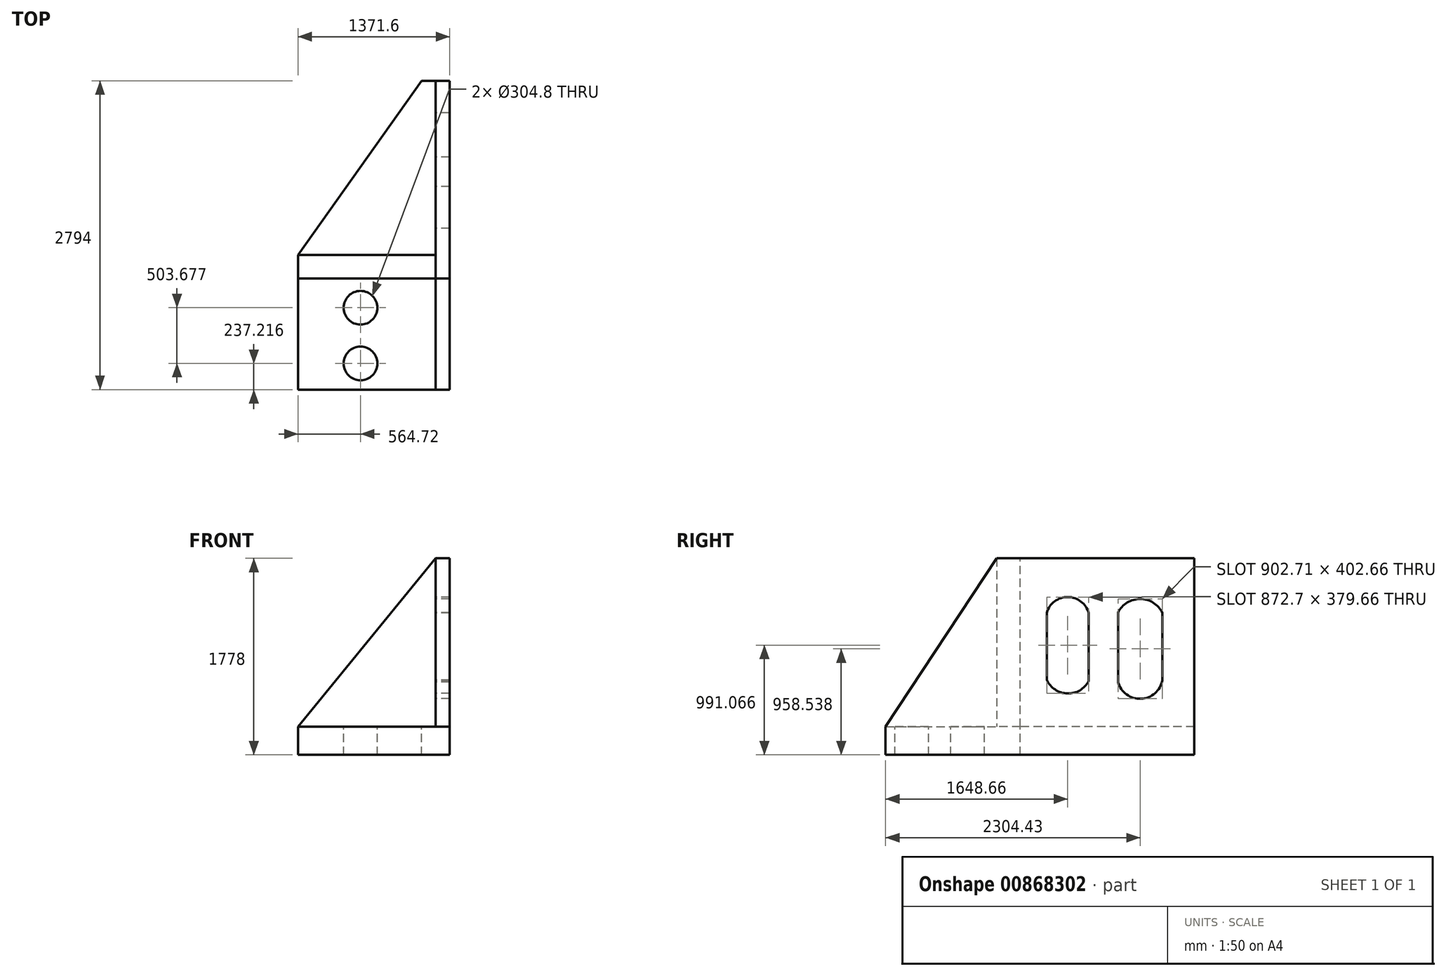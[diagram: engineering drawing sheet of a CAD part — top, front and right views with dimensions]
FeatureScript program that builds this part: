
annotation { "Feature Type Name" : "Feature", "Feature Type Description" : "" }
export const myFeature = defineFeature(function(context is Context, id is Id, definition is map)
    precondition{}
    {
        {
            var Q0;
            Q0=qCreatedBy(makeId("Top.planeOp"),FACE);
            var sketch = newSketch(context, id + "F0", { "sketchPlane" : qUnion([Q0])});
            skLineSegment(sketch, "E0.bottom", {"start": v(254, 1574.8) * mm, "end": v(0, 1574.8) * mm});
            skLineSegment(sketch, "E0.top", {"start": v(254, -1219.2) * mm, "end": v(-1117.6, -1219.2) * mm});
            skLineSegment(sketch, "E0.left", {"start": v(254, 1574.8) * mm, "end": v(254, -1219.2) * mm});
            skLineSegment(sketch, "E0.right", {"start": v(-1117.6, 0) * mm, "end": v(-1117.6, -1219.2) * mm});
            skLineSegment(sketch, "E1", {"start": v(0, 1574.8) * mm, "end": v(-1117.6, 0) * mm});
            skPoint(sketch, "E2.end.orphan", {"position": v(0, 1309.87) * mm});
            skPoint(sketch, "E3.end.orphan", {"position": v(-468.45, -609.6) * mm});
            skPoint(sketch, "E4.orphan", {"position": v(-468.45, -1219.2) * mm});
            skPoint(sketch, "E5.end.orphan", {"position": v(-468.45, 0) * mm});
            skCircle(sketch, "E6", {"center": v(-552.88, -478.3) * mm, "radius": 152.4 * mm});
            skCircle(sketch, "E7", {"center": v(-552.88, -981.98) * mm, "radius": 152.4 * mm});
            skSolve(sketch);
        }
        {
            var Q0;
            Q0=makeQuery(id+"F0.imprint","IMPRINT",FACE,{"disambiguationData":[TD([[makeQuery(id+"F0.imprint","IMPRINT",EDGE,{"derivedFrom":sQuery(id+"F0.wireOp",EDGE,"E0.bottom")}),1.0]])]});
            extrude(context, id + "F1", {"entities" : qUnion([Q0]), "oppositeDirection" : true, "depth" : 254 * mm, "offsetDistance" : 25.4 * mm});
        }
        {
            var Q0;
            Q0=makeQuery(id+"F1.opExtrude","CAP_FACE",FACE,{"disambiguationData":[OSD([sQuery(id+"F0.wireOp",EDGE,"E0.bottom"),sQuery(id+"F0.wireOp",EDGE,"E0.top"),sQuery(id+"F0.wireOp",EDGE,"E0.left"),sQuery(id+"F0.wireOp",EDGE,"E0.right"),sQuery(id+"F0.wireOp",EDGE,"E1"),sQuery(id+"F0.wireOp",EDGE,"E6"),sQuery(id+"F0.wireOp",EDGE,"E7")])],"isStart":true});
            var sketch = newSketch(context, id + "F2", { "sketchPlane" : qUnion([Q0])});
            skLineSegment(sketch, "E8", {"start": v(-1117.6, 0) * mm, "end": v(127, 0) * mm});
            skLineSegment(sketch, "E9", {"start": v(-431.8, -213.73) * mm, "end": v(-1117.6, -213.73) * mm});
            skLineSegment(sketch, "E10", {"start": v(-1117.6, -213.73) * mm, "end": v(127, -213.73) * mm});
            skPoint(sketch, "E11.start.orphan", {"position": v(-431.8, 0) * mm});
            skLineSegment(sketch, "E12", {"start": v(127, 1574.8) * mm, "end": v(127, 0) * mm});
            skPoint(sketch, "E13.orphan", {"position": v(254, 0) * mm});
            skLineSegment(sketch, "E14", {"start": v(127, -1219.2) * mm, "end": v(127, -213.73) * mm});
            skLineSegment(sketch, "E15", {"start": v(127, -213.73) * mm, "end": v(254, -213.73) * mm});
            skLineSegment(sketch, "E16", {"start": v(254, -213.73) * mm, "end": v(254, 0) * mm});
            skLineSegment(sketch, "E17", {"start": v(127, 0) * mm, "end": v(127, -213.73) * mm});
            skSolve(sketch);
        }
        {
            var Q0;
            {var subQ1=sQuery(id+"F2.wireOp",EDGE,"E8");Q0=makeQuery(id+"F2.imprint","IMPRINT",FACE,{"disambiguationData":[TD([[makeQuery(id+"F2.imprint","IMPRINT",EDGE,{"derivedFrom":subQ1}),-1.0]])]});}
            var Q1;
            {var subQ0=sQuery(id+"F2.wireOp",EDGE,"E14");Q1=makeQuery(id+"F2.imprint","IMPRINT",FACE,{"disambiguationData":[TD([[makeQuery(id+"F2.imprint","IMPRINT",EDGE,{"derivedFrom":subQ0}),-1.0]])]});}
            var Q2;
            {var subQ1=sQuery(id+"F2.wireOp",EDGE,"E12");Q2=makeQuery(id+"F2.imprint","IMPRINT",FACE,{"disambiguationData":[TD([[makeQuery(id+"F2.imprint","IMPRINT",EDGE,{"derivedFrom":subQ1}),1.0]])]});}
            extrude(context, id + "F3", {"entities" : qUnion([Q0, Q1, Q2]), "operationType" : NewBodyOperationType.ADD, "depth" : 1524 * mm, "offsetDistance" : 25.4 * mm});
        }
        {
            var Q0;
            Q0=makeQuery(id+"F3.opExtrude","SWEPT_FACE",FACE,{"disambiguationData":[OSD([sQuery(id+"F2.wireOp",EDGE,"E12")])]});
            var sketch = newSketch(context, id + "F4", { "sketchPlane" : qUnion([Q0])});
            skArc(sketch, "E18", {"start": v(-883.9, 1033.35) * mm, "mid": v(-1086.12, 1155.9) * mm, "end": v(-1286.57, 1030.47) * mm});
            skArc(sketch, "E19", {"start": v(-239.64, 1030.47) * mm, "mid": v(-430.56, 1173.42) * mm, "end": v(-619.3, 1027.6) * mm});
            skArc(sketch, "E20", {"start": v(-619.3, 412.1) * mm, "mid": v(-425.92, 300.71) * mm, "end": v(-239.64, 423.6) * mm});
            skArc(sketch, "E21", {"start": v(-1286.57, 420.72) * mm, "mid": v(-1092.04, 253.18) * mm, "end": v(-883.9, 403.47) * mm});
            skLineSegment(sketch, "E22", {"start": v(-1286.57, 1030.47) * mm, "end": v(-1286.57, 420.72) * mm});
            skLineSegment(sketch, "E23", {"start": v(-883.9, 1033.35) * mm, "end": v(-883.9, 403.47) * mm});
            skLineSegment(sketch, "E24", {"start": v(-619.3, 1027.6) * mm, "end": v(-619.3, 412.1) * mm});
            skLineSegment(sketch, "E25", {"start": v(-239.64, 423.6) * mm, "end": v(-239.64, 1030.47) * mm});
            skSolve(sketch);
        }
        {
            var Q0;
            Q0=makeQuery(id+"F3.opExtrude","SWEPT_FACE",FACE,{"disambiguationData":[OSD([sQuery(id+"F2.wireOp",EDGE,"E14")])]});
            var sketch = newSketch(context, id + "F5", { "sketchPlane" : qUnion([Q0])});
            skLineSegment(sketch, "E26", {"start": v(213.73, 1524) * mm, "end": v(1219.2, 0) * mm});
            skLineSegment(sketch, "E27", {"start": v(1219.2, 0) * mm, "end": v(1219.2, 1524) * mm});
            skLineSegment(sketch, "E28", {"start": v(1219.2, 1524) * mm, "end": v(213.73, 1524) * mm});
            skPoint(sketch, "E29.end.orphan", {"position": v(0, 1396.86) * mm});
            skSolve(sketch);
        }
        {
            var Q0;
            Q0=makeQuery(id+"F5.imprint","IMPRINT",FACE,{"disambiguationData":[TD([[makeQuery(id+"F5.imprint","IMPRINT",EDGE,{"derivedFrom":sQuery(id+"F5.wireOp",EDGE,"E26")}),1.0]])]});
            extrude(context, id + "F6", {"entities" : qUnion([Q0]), "operationType" : NewBodyOperationType.REMOVE, "oppositeDirection" : true, "depth" : 254 * mm, "offsetDistance" : 25.4 * mm});
        }
        {
            var Q0;
            Q0=makeQuery(id+"F3.opExtrude","SWEPT_FACE",FACE,{"disambiguationData":[OSD([sQuery(id+"F2.wireOp",EDGE,"E10")])]});
            var sketch = newSketch(context, id + "F7", { "sketchPlane" : qUnion([Q0])});
            skLineSegment(sketch, "E30", {"start": v(127, 1524) * mm, "end": v(-1117.6, 0) * mm});
            skLineSegment(sketch, "E31", {"start": v(-1117.6, 0) * mm, "end": v(-1117.6, 1524) * mm});
            skLineSegment(sketch, "E32", {"start": v(-1117.6, 1524) * mm, "end": v(127, 1524) * mm});
            skSolve(sketch);
        }
        {
            var Q0;
            Q0 = qSketchRegion(id + "F7", true);
            extrude(context, id + "F8", {"entities" : qUnion([Q0]), "operationType" : NewBodyOperationType.REMOVE, "oppositeDirection" : true, "depth" : 254 * mm, "offsetDistance" : 25.4 * mm});
        }
        {
            var Q0;
            Q0=makeQuery(id+"F4.imprint","IMPRINT",FACE,{"disambiguationData":[TD([[makeQuery(id+"F4.imprint","IMPRINT",EDGE,{"derivedFrom":sQuery(id+"F4.wireOp",EDGE,"E18")}),1.0]])]});
            var Q1;
            Q1=makeQuery(id+"F4.imprint","IMPRINT",FACE,{"disambiguationData":[TD([[makeQuery(id+"F4.imprint","IMPRINT",EDGE,{"derivedFrom":sQuery(id+"F4.wireOp",EDGE,"E19")}),1.0]])]});
            extrude(context, id + "F9", {"entities" : qUnion([Q0, Q1]), "operationType" : NewBodyOperationType.REMOVE, "oppositeDirection" : true, "depth" : 254 * mm, "offsetDistance" : 25.4 * mm});
        }
    });
